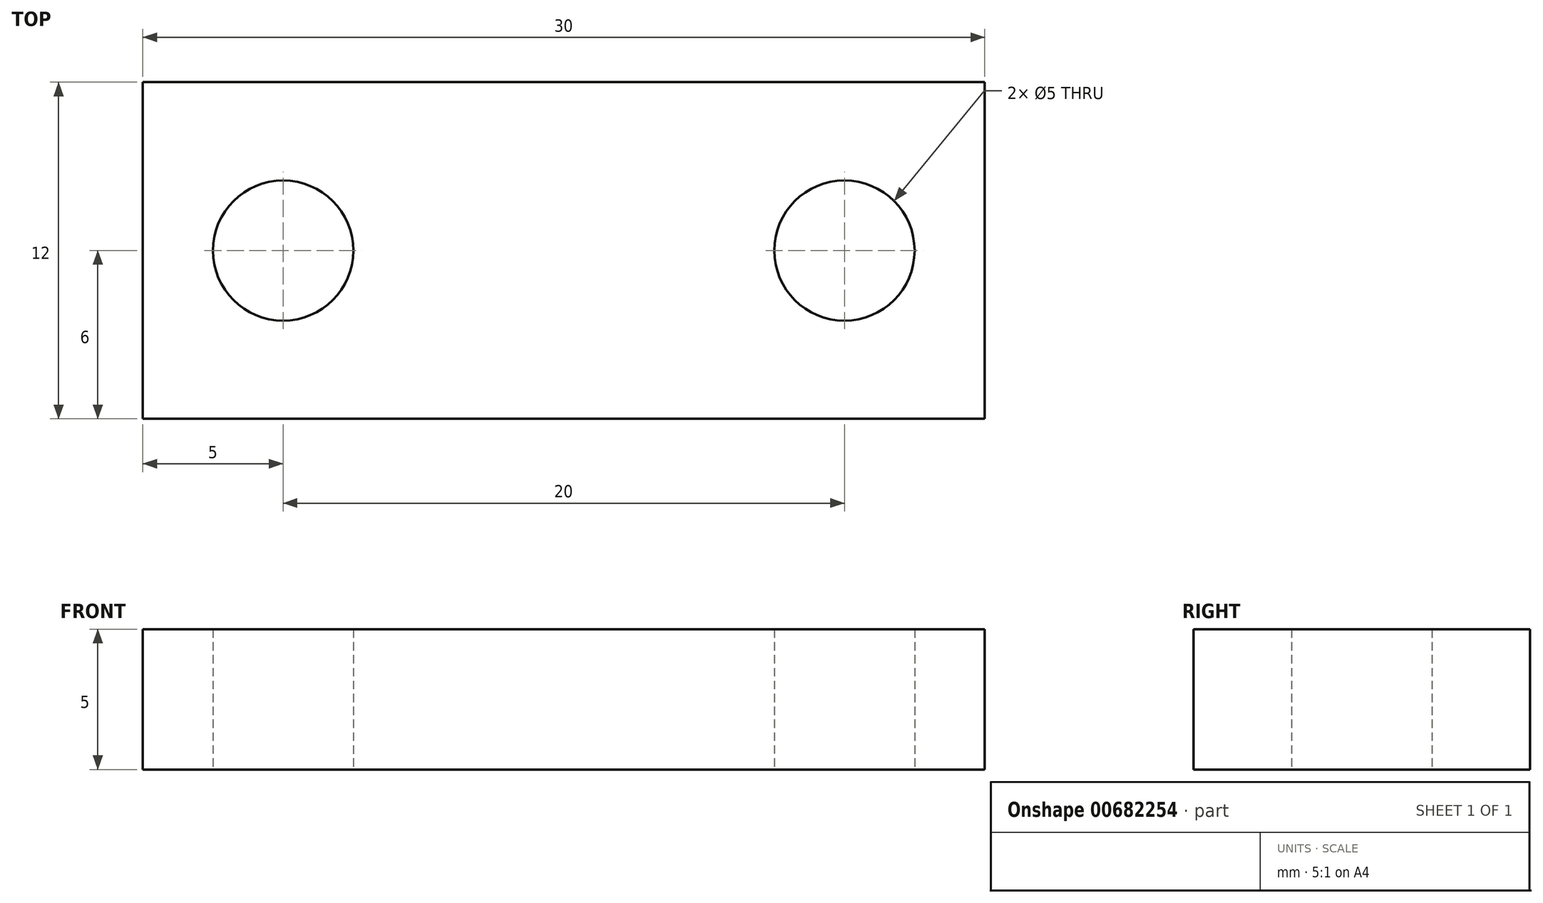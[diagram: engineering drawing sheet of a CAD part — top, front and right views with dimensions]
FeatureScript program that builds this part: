
annotation { "Feature Type Name" : "Feature", "Feature Type Description" : "" }
export const myFeature = defineFeature(function(context is Context, id is Id, definition is map)
    precondition{}
    {
        {
            var Q0;
            Q0=qCreatedBy(makeId("Top.planeOp"),FACE);
            var sketch = newSketch(context, id + "F0", { "sketchPlane" : qUnion([Q0])});
            skLineSegment(sketch, "E0.bottom", {"start": v(15, -6) * mm, "end": v(-15, -6) * mm});
            skLineSegment(sketch, "E0.top", {"start": v(15, 6) * mm, "end": v(-15, 6) * mm});
            skLineSegment(sketch, "E0.left", {"start": v(15, -6) * mm, "end": v(15, 6) * mm});
            skLineSegment(sketch, "E0.right", {"start": v(-15, -6) * mm, "end": v(-15, 6) * mm});
            skPoint(sketch, "E0.middle", {"position": v(0, 0) * mm});
            skCircle(sketch, "E1", {"center": v(-10, 0) * mm, "radius": 2.5 * mm});
            skCircle(sketch, "E2", {"center": v(10, 0) * mm, "radius": 2.5 * mm});
            skLineSegment(sketch, "E3", {"start": v(0, 6) * mm, "end": v(0, -6) * mm});
            skSolve(sketch);
        }
        {
            var Q0;
            Q0 = qSketchRegion(id + "F0", true);
            extrude(context, id + "F1", {"entities" : qUnion([Q0]), "depth" : 5 * mm, "offsetDistance" : 25 * mm});
        }
    });
